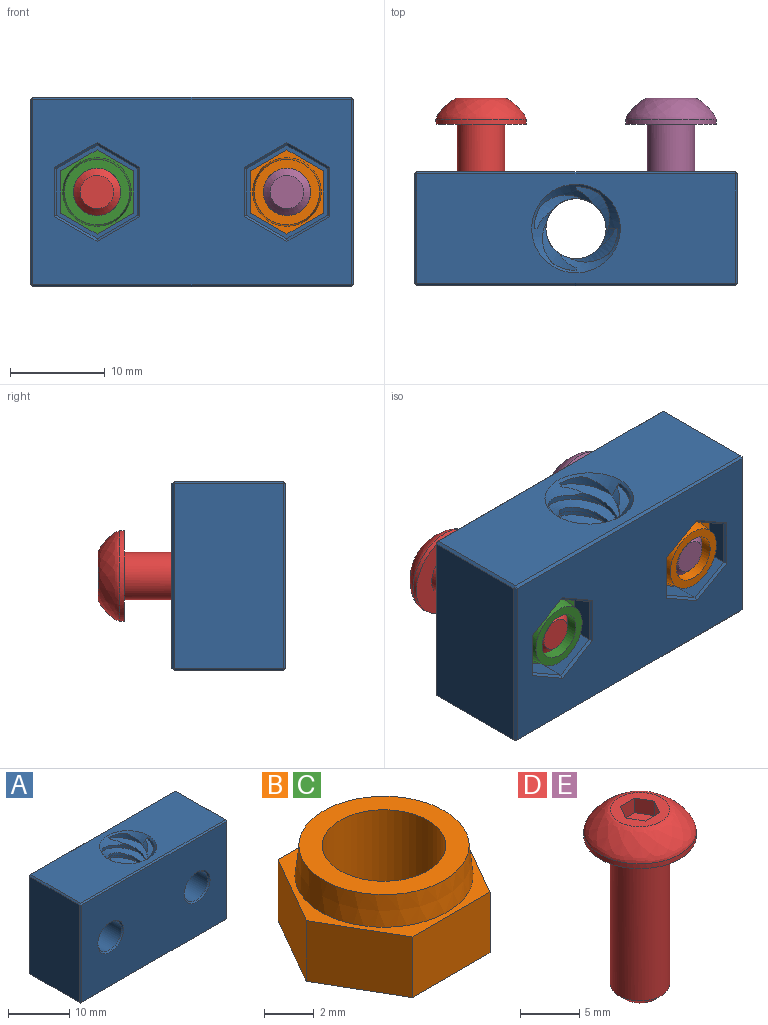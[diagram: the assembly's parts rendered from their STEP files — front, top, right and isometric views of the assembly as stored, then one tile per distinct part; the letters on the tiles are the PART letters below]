
ASSEMBLY  parts=5 mates=1
PART A: 84 faces, bbox 34x12x21.5 mm
  f0: bspline ~20.25x8.84mm, area 73.1mm2, adj f1,f18,f20,f81,f82
  f1: cylinder r=4.42mm len=19.5mm, axis (0,0,-1), area 67.9mm2, adj f0,f2,f12,f20,f80,f82
  f2: bspline ~20.25x8.84mm, area 73.1mm2, adj f1,f12,f19,f80,f82
  f3: bspline ~20.25x8.84mm, area 73.1mm2, adj f4,f17,f21,f80,f82,f83
  f4: cylinder r=4.42mm len=19.5mm, axis (0,0,-1), area 67.9mm2, adj f3,f5,f13,f21,f80,f82
  f5: bspline ~20.25x8.84mm, area 73.1mm2, adj f4,f13,f18,f80,f81,f82
  f6: bspline ~20.25x8.84mm, area 73.1mm2, adj f7,f16,f22,f80,f82
  f7: cylinder r=4.42mm len=19.5mm, axis (0,0,-1), area 67.9mm2, adj f6,f8,f14,f22,f80,f82
  f8: bspline ~20.25x8.84mm, area 73.1mm2, adj f7,f14,f17,f80,f83
  f9: bspline ~20.25x8.84mm, area 73.1mm2, adj f10,f19,f23,f80,f82
  f10: cylinder r=4.42mm len=19.5mm, axis (0,0,-1), area 67.9mm2, adj f9,f11,f15,f23,f80,f82
  f11: bspline ~20.25x8.84mm, area 73.1mm2, adj f10,f15,f16,f80,f82
  f12: plane 0.31x0.31mm, normal (0,-1,0), area 0mm2, adj f1,f2,f82
  f13: plane 0.31x0.31mm, normal (1,0,0), area 0mm2, adj f4,f5,f82
  f14: plane 0.31x0.31mm, normal (0,1,0), area 0mm2, adj f7,f8,f82
  f15: plane 0.31x0.31mm, normal (-1,0,0), area 0mm2, adj f10,f11,f82
  f16: cylinder r=3.17mm len=17mm, axis (0,0,-1), area 21.1mm2, adj f6,f11,f80,f82
  f17: cylinder r=3.17mm len=17mm, axis (0,0,-1), area 21.1mm2, adj f3,f8,f80,f83
  f18: cylinder r=3.17mm len=17mm, axis (0,0,-1), area 21.1mm2, adj f0,f5,f81,f82
  f19: cylinder r=3.17mm len=17mm, axis (0,0,-1), area 21.1mm2, adj f2,f9,f80,f82
  f20: plane 0.31x0.31mm, normal (0,-1,0), area 0mm2, adj f0,f1,f80
  f21: plane 0.31x0.31mm, normal (1,0,0), area 0mm2, adj f3,f4,f80
  f22: plane 0.31x0.31mm, normal (0,1,0), area 0mm2, adj f6,f7,f80
  f23: plane 0.31x0.31mm, normal (-1,0,0), area 0mm2, adj f9,f10,f80
  f24: plane 33.5x11.5mm, normal (0,0,1), area 316.8mm2, adj f54,f59,f62,f65,f80
  f25: plane 33.5x19.5mm, normal (0,1,0), area 513mm2, adj f49,f50,f59,f60,f68,f69,f70,f71
  f26: cylinder r=2.75mm len=6.75mm, axis (0,-1,0), area 116.6mm2, adj f39,f67
  f27: cylinder r=2.75mm len=6.75mm, axis (0,-1,0), area 116.6mm2, adj f32,f66
  f28: plane 33.5x19.5mm, normal (0,-1,0), area 596.7mm2, adj f52,f53,f61,f62,f66,f67
  f29: plane 19.5x11.5mm, normal (1,0,0), area 224.2mm2, adj f51,f60,f61,f65
  f30: plane 19.5x11.5mm, normal (-1,0,0), area 224.2mm2, adj f46,f49,f53,f54
  f31: plane 33.5x11.5mm, normal (0,0,-1), area 316.8mm2, adj f46,f50,f51,f52,f82
  f32: plane 9.82x8.5mm, normal (0,1,0), area 38.8mm2, adj f27,f33,f34,f35,f36,f37,f38
  f33: plane 4.75x4.25mm, normal (0.5,0,-0.87), area 23.3mm2, adj f32,f34,f38,f71
  f34: plane 4.75x4.25mm, normal (-0.5,0,-0.87), area 23.3mm2, adj f32,f33,f35,f73
  f35: plane 4.91x4.75mm, normal (-1,0,0), area 23.3mm2, adj f32,f34,f36,f72
  f36: plane 4.75x4.25mm, normal (-0.5,0,0.87), area 23.3mm2, adj f32,f35,f37,f70
  f37: plane 4.75x4.25mm, normal (0.5,0,0.87), area 23.3mm2, adj f32,f36,f38,f68
  f38: plane 4.91x4.75mm, normal (1,0,0), area 23.3mm2, adj f32,f33,f37,f69
  f39: plane 9.82x8.5mm, normal (0,1,0), area 38.8mm2, adj f26,f40,f41,f42,f43,f44,f45
  f40: plane 4.91x4.75mm, normal (-1,0,0), area 23.3mm2, adj f39,f41,f45,f79
  f41: plane 4.75x4.25mm, normal (-0.5,0,0.87), area 23.3mm2, adj f39,f40,f42,f77
  f42: plane 4.75x4.25mm, normal (0.5,0,0.87), area 23.3mm2, adj f39,f41,f43,f75
  f43: plane 4.91x4.75mm, normal (1,0,0), area 23.3mm2, adj f39,f42,f44,f74
  f44: plane 4.75x4.25mm, normal (0.5,0,-0.87), area 23.3mm2, adj f39,f43,f45,f76
  f45: plane 4.75x4.25mm, normal (-0.5,0,-0.87), area 23.3mm2, adj f39,f40,f44,f78
  f46: plane 11.5x0.25mm, normal (-0.71,0,-0.71), area 4.1mm2, adj f30,f31,f47,f48
  f47: plane 0.25x0.25mm, normal (-0.58,0.58,-0.58), area 0.1mm2, adj f46,f49,f50
  f48: plane 0.25x0.25mm, normal (-0.58,-0.58,-0.58), area 0.1mm2, adj f46,f52,f53
  f49: plane 19.5x0.25mm, normal (-0.71,0.71,0), area 6.9mm2, adj f25,f30,f47,f55
  f50: plane 33.5x0.25mm, normal (0,0.71,-0.71), area 11.8mm2, adj f25,f31,f47,f56
  f51: plane 11.5x0.25mm, normal (0.71,0,-0.71), area 4.1mm2, adj f29,f31,f56,f57
  f52: plane 33.5x0.25mm, normal (0,-0.71,-0.71), area 11.8mm2, adj f28,f31,f48,f57
  f53: plane 19.5x0.25mm, normal (-0.71,-0.71,0), area 6.9mm2, adj f28,f30,f48,f58
  f54: plane 11.5x0.25mm, normal (-0.71,0,0.71), area 4.1mm2, adj f24,f30,f55,f58
  f55: plane 0.25x0.25mm, normal (-0.58,0.58,0.58), area 0.1mm2, adj f49,f54,f59
  f56: plane 0.25x0.25mm, normal (0.58,0.58,-0.58), area 0.1mm2, adj f50,f51,f60
  f57: plane 0.25x0.25mm, normal (0.58,-0.58,-0.58), area 0.1mm2, adj f51,f52,f61
  f58: plane 0.25x0.25mm, normal (-0.58,-0.58,0.58), area 0.1mm2, adj f53,f54,f62
  f59: plane 33.5x0.25mm, normal (0,0.71,0.71), area 11.8mm2, adj f24,f25,f55,f63
  f60: plane 19.5x0.25mm, normal (0.71,0.71,0), area 6.9mm2, adj f25,f29,f56,f63
  f61: plane 19.5x0.25mm, normal (0.71,-0.71,0), area 6.9mm2, adj f28,f29,f57,f64
  f62: plane 33.5x0.25mm, normal (0,-0.71,0.71), area 11.8mm2, adj f24,f28,f58,f64
  f63: plane 0.25x0.25mm, normal (0.58,0.58,0.58), area 0.1mm2, adj f59,f60,f65
  f64: plane 0.25x0.25mm, normal (0.58,-0.58,0.58), area 0.1mm2, adj f61,f62,f65
  f65: plane 11.5x0.25mm, normal (0.71,0,0.71), area 4.1mm2, adj f24,f29,f63,f64
  f66: cone r=2.75mm half-angle=45deg, axis (0,-1,0), area 6.4mm2, adj f27,f28
  f67: cone r=2.75mm half-angle=45deg, axis (0,-1,0), area 6.4mm2, adj f26,f28
  f68: plane 4.5x2.74mm, normal (0.35,0.71,0.61), area 1.8mm2, adj f25,f37,f69,f70
  f69: plane 5.2x0.25mm, normal (0.71,0.71,0), area 1.8mm2, adj f25,f38,f68,f71
  f70: plane 4.5x2.74mm, normal (-0.35,0.71,0.61), area 1.8mm2, adj f25,f36,f68,f72
  f71: plane 4.5x2.74mm, normal (0.35,0.71,-0.61), area 1.8mm2, adj f25,f33,f69,f73
  f72: plane 5.2x0.25mm, normal (-0.71,0.71,0), area 1.8mm2, adj f25,f35,f70,f73
  f73: plane 4.5x2.74mm, normal (-0.35,0.71,-0.61), area 1.8mm2, adj f25,f34,f71,f72
  f74: plane 5.2x0.25mm, normal (0.71,0.71,0), area 1.8mm2, adj f25,f43,f75,f76
  f75: plane 4.5x2.74mm, normal (0.35,0.71,0.61), area 1.8mm2, adj f25,f42,f74,f77
  f76: plane 4.5x2.74mm, normal (0.35,0.71,-0.61), area 1.8mm2, adj f25,f44,f74,f78
  f77: plane 4.5x2.74mm, normal (-0.35,0.71,0.61), area 1.8mm2, adj f25,f41,f75,f79
  f78: plane 4.5x2.74mm, normal (-0.35,0.71,-0.61), area 1.8mm2, adj f25,f45,f76,f79
  f79: plane 5.2x0.25mm, normal (-0.71,0.71,0), area 1.8mm2, adj f25,f40,f77,f78
  f80: cone r=3.17mm half-angle=45deg, axis (0,0,1), area 25.6mm2, adj f1,f2,f3,f4,f5,f6,f7,f8
  f81: cone r=3.17mm half-angle=45deg, axis (0,0,1), area 1.3mm2, adj f0,f5,f18,f80
  f82: cone r=3.17mm half-angle=45deg, axis (0,0,-1), area 25.6mm2, adj f0,f1,f2,f3,f4,f5,f6,f7
  f83: cone r=3.17mm half-angle=45deg, axis (0,0,-1), area 1.3mm2, adj f3,f8,f17,f82
PART B: 11 faces, bbox 8.9x7.7x4.5 mm
  f0: plane 3.84x3mm, normal (-0.87,0.5,0), area 13.3mm2, adj f1,f5,f6,f7
  f1: plane 3.84x3mm, normal (-0.87,-0.5,0), area 13.3mm2, adj f0,f2,f6,f7
  f2: plane 4.43x3mm, normal (0,-1,0), area 13.3mm2, adj f1,f3,f6,f7
  f3: plane 3.84x3mm, normal (0.87,-0.5,0), area 13.3mm2, adj f2,f4,f6,f7
  f4: plane 3.84x3mm, normal (0.87,0.5,0), area 13.3mm2, adj f3,f5,f6,f7
  f5: plane 4.43x3mm, normal (0,1,0), area 13.3mm2, adj f0,f4,f6,f7
  f6: plane 8.87x7.68mm, normal (0,0,1), area 10.4mm2, adj f0,f1,f2,f3,f4,f5,f8
  f7: plane 8.87x7.68mm, normal (0,0,-1), area 31.4mm2, adj f0,f1,f2,f3,f4,f5,f10
  f8: cone r=3.6mm half-angle=6deg, axis (0,0,-1), area 33.4mm2, adj f6,f9
  f9: plane 6.88x6.88mm, normal (0,0,1), area 17.6mm2, adj f8,f10
  f10: cylinder r=2.5mm len=5mm, axis (0,0,1), area 70.7mm2, adj f7,f9
PART C: same geometry as B
PART D: 14 faces, bbox 9.5x9.5x18.8 mm
  f0: plane 5.01x5.01mm, normal (0,0,1), area 11.8mm2, adj f3,f4,f5,f6,f7,f8,f10
  f1: cylinder r=4.75mm len=9.5mm, axis (0,0,-1), area 14.9mm2, adj f2,f10
  f2: plane 9.5x9.5mm, normal (0,0,-1), area 51.2mm2, adj f1,f11
  f3: plane 1.5x1.5mm, normal (-0.87,-0.5,0), area 2.6mm2, adj f0,f4,f8,f9
  f4: plane 1.73x1.5mm, normal (0,-1,0), area 2.6mm2, adj f0,f3,f5,f9
  f5: plane 1.5x1.5mm, normal (0.87,-0.5,0), area 2.6mm2, adj f0,f4,f6,f9
  f6: plane 1.5x1.5mm, normal (0.87,0.5,0), area 2.6mm2, adj f0,f5,f7,f9
  f7: plane 1.73x1.5mm, normal (0,1,0), area 2.6mm2, adj f0,f6,f8,f9
  f8: plane 1.5x1.5mm, normal (-0.87,0.5,0), area 2.6mm2, adj f0,f3,f7,f9
  f9: plane 3.46x3mm, normal (0,0,1), area 7.8mm2, adj f3,f4,f5,f6,f7,f8
  f10: bspline ~9.5x9.5mm, area 78.3mm2, adj f0,f1
  f11: cylinder r=2.5mm len=15.25mm, axis (0,0,1), area 239.5mm2, adj f2,f13
  f12: plane 3.5x3.5mm, normal (0,0,-1), area 9.6mm2, adj f13
  f13: cone r=1.75mm half-angle=45deg, axis (0,0,1), area 14.2mm2, adj f11,f12
PART E: same geometry as D
PLACE A rot(axis=(1,0,0),180deg) t=(-35.32,-6,-54.47)mm
PLACE B rot(axis=(0.58,-0.58,0.58),120deg) t=(-25.32,-7,-64.47)mm
PLACE C rot(axis=(0.58,-0.58,0.58),120deg) t=(-45.32,-7,-64.47)mm
PLACE D rot(axis=(-1,0,0),90deg) t=(-20.32,5,-64.47)mm
PLACE E rot(axis=(-1,0,0),90deg) t=(-0.32,5,-64.47)mm
MATE fastened C.f8 <-> A.f26  axis (0,1,0) through (-45.32,-7,-64.47)mm
